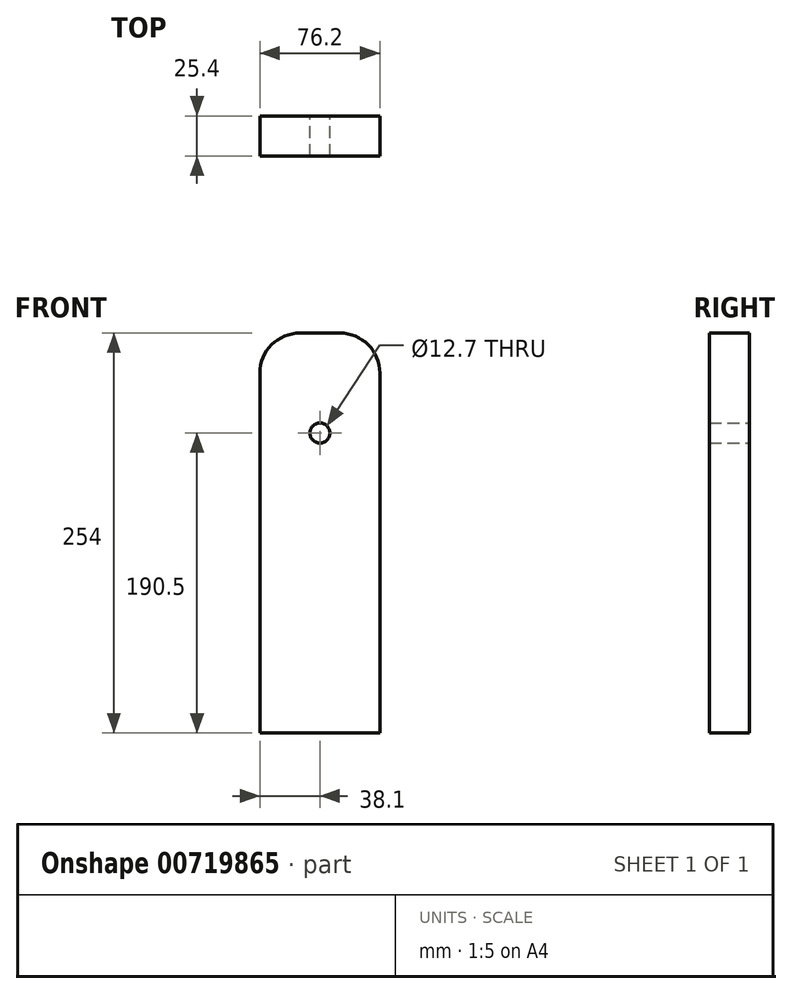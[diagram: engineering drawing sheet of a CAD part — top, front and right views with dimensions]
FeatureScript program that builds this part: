
annotation { "Feature Type Name" : "Feature", "Feature Type Description" : "" }
export const myFeature = defineFeature(function(context is Context, id is Id, definition is map)
    precondition{}
    {
        {
            var Q0;
            Q0=qCreatedBy(makeId("Top.planeOp"),FACE);
            var sketch = newSketch(context, id + "F0", { "sketchPlane" : qUnion([Q0])});
            skLineSegment(sketch, "E0.bottom", {"start": v(76.2, 28.37) * mm, "end": v(0, 28.37) * mm});
            skLineSegment(sketch, "E0.top", {"start": v(76.2, 53.77) * mm, "end": v(0, 53.77) * mm});
            skLineSegment(sketch, "E0.left", {"start": v(76.2, 28.37) * mm, "end": v(76.2, 53.77) * mm});
            skLineSegment(sketch, "E0.right", {"start": v(0, 28.37) * mm, "end": v(0, 53.77) * mm});
            skSolve(sketch);
        }
        {
            var Q0;
            Q0=makeQuery(id+"F0.imprint","IMPRINT",FACE,{"disambiguationData":[TD([[makeQuery(id+"F0.imprint","IMPRINT",EDGE,{"derivedFrom":sQuery(id+"F0.wireOp",EDGE,"E0.bottom")}),-1.0]])]});
            extrude(context, id + "F1", {"entities" : qUnion([Q0]), "depth" : 254 * mm, "offsetDistance" : 25.4 * mm});
        }
        {
            var Q0;
            Q0=makeQuery(id+"F1.opExtrude","CAP_EDGE",EDGE,{"disambiguationData":[OSD([sQuery(id+"F0.wireOp",EDGE,"E0.right")])],"isStart":false});
            var Q1;
            Q1=makeQuery(id+"F1.opExtrude","CAP_EDGE",EDGE,{"disambiguationData":[OSD([sQuery(id+"F0.wireOp",EDGE,"E0.left")])],"isStart":false});
            fillet(context, id + "F2", {"entities" : qUnion([Q0, Q1]), "radius" : 25.4 * mm, "tangentPropagation" : true, "allowEdgeOverflow" : false});
        }
        {
            var Q0;
            Q0=makeQuery(id+"F1.opExtrude","SWEPT_FACE",FACE,{"disambiguationData":[OSD([sQuery(id+"F0.wireOp",EDGE,"E0.top")])]});
            var sketch = newSketch(context, id + "F3", { "sketchPlane" : qUnion([Q0])});
            skCircle(sketch, "E1", {"center": v(-38.1, 190.5) * mm, "radius": 6.35 * mm});
            skSolve(sketch);
        }
        {
            var Q0;
            Q0=sQuery(id+"F3.wireOp",VERTEX,"E1.center");
            var Q1;
            Q1=makeQuery(id+"F1.opExtrude","SWEPT_BODY",BODY,{"disambiguationData":[OSD([sQuery(id+"F0.wireOp",EDGE,"E0.bottom"),sQuery(id+"F0.wireOp",EDGE,"E0.top"),sQuery(id+"F0.wireOp",EDGE,"E0.left"),sQuery(id+"F0.wireOp",EDGE,"E0.right")])]});
            hole(context, id + "F4", {"style" : HoleStyle.SIMPLE, "endStyle" : HoleEndStyle.THROUGH, "holeDiameter" : 12.7 * mm, "majorDiameter" : 6.35 * mm, "isTappedThrough" : true, "tappedDepth" : 12.7 * mm, "tapClearance" : 3, "locations" : qUnion([Q0]), "scope" : qUnion([Q1])});
        }
    });
